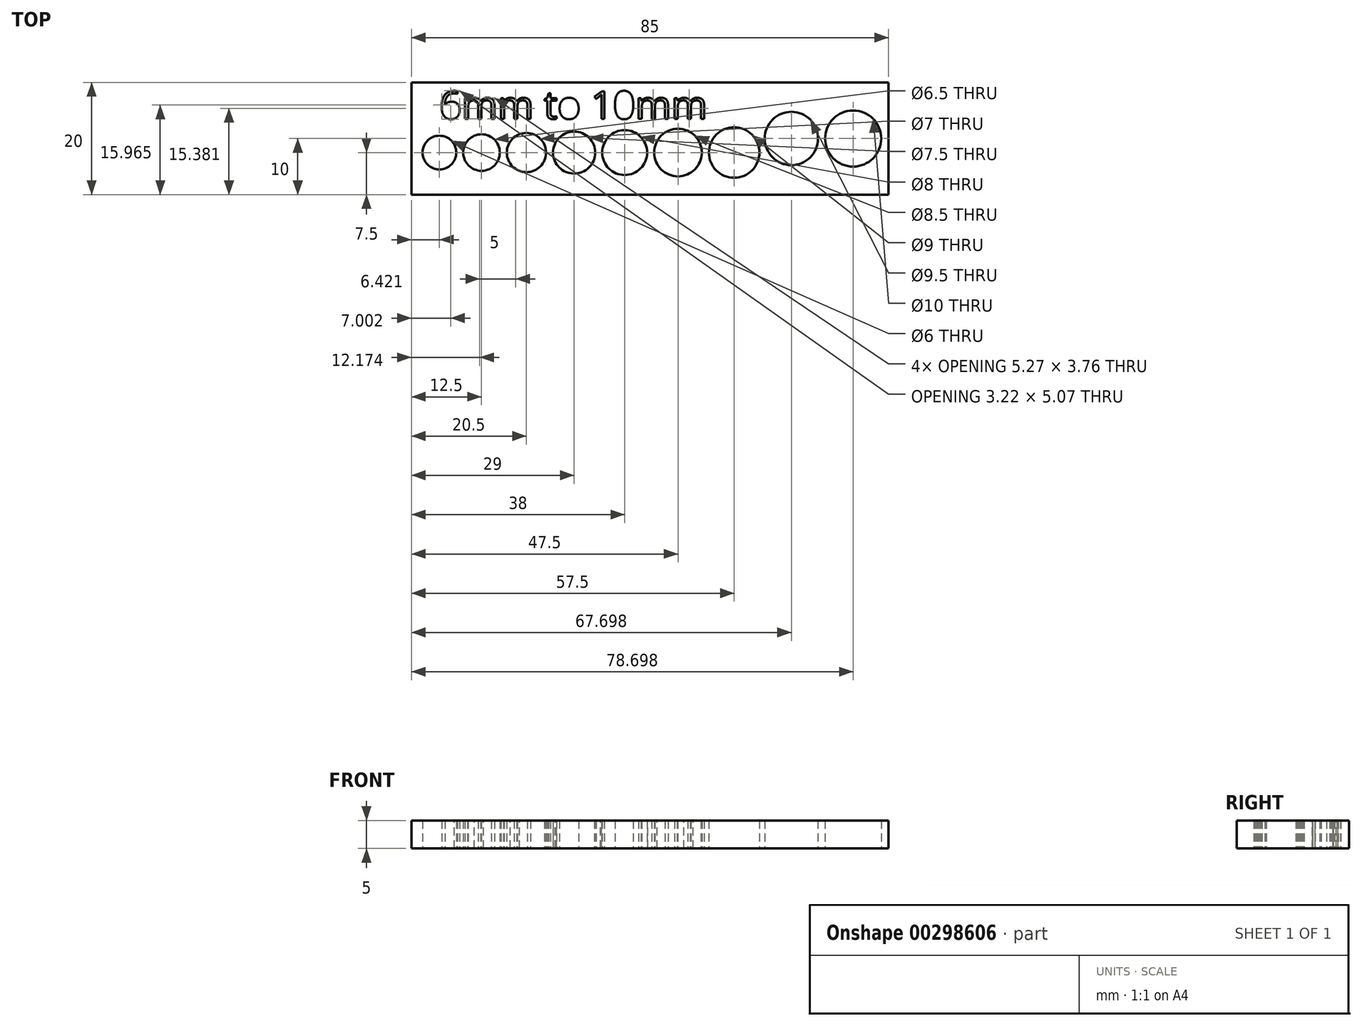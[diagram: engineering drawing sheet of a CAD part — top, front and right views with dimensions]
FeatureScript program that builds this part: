
annotation { "Feature Type Name" : "Feature", "Feature Type Description" : "" }
export const myFeature = defineFeature(function(context is Context, id is Id, definition is map)
    precondition{}
    {
        {
            var Q0;
            Q0=qCreatedBy(makeId("Top.planeOp"),FACE);
            var sketch = newSketch(context, id + "F0", { "sketchPlane" : qUnion([Q0])});
            skLineSegment(sketch, "E0.bottom", {"start": v(0, 0) * mm, "end": v(85, 0) * mm});
            skLineSegment(sketch, "E0.top", {"start": v(0, 20) * mm, "end": v(85, 20) * mm});
            skLineSegment(sketch, "E0.left", {"start": v(0, 0) * mm, "end": v(0, 20) * mm});
            skLineSegment(sketch, "E0.right", {"start": v(85, 0) * mm, "end": v(85, 20) * mm});
            skLineSegment(sketch, "E1", {"start": v(0, 7.5) * mm, "end": v(5, 7.5) * mm});
            skLineSegment(sketch, "E2", {"start": v(5, 7.5) * mm, "end": v(5, 0) * mm});
            skCircle(sketch, "E3", {"center": v(5, 7.5) * mm, "radius": 3 * mm});
            skLineSegment(sketch, "E4", {"start": v(5, 7.5) * mm, "end": v(12.5, 7.5) * mm});
            skLineSegment(sketch, "E5", {"start": v(12.5, 7.5) * mm, "end": v(20.5, 7.5) * mm});
            skLineSegment(sketch, "E6", {"start": v(20.5, 7.5) * mm, "end": v(29, 7.5) * mm});
            skCircle(sketch, "E7", {"center": v(12.5, 7.5) * mm, "radius": 3.25 * mm});
            skCircle(sketch, "E8", {"center": v(20.5, 7.5) * mm, "radius": 3.5 * mm});
            skCircle(sketch, "E9", {"center": v(29, 7.5) * mm, "radius": 3.75 * mm});
            skLineSegment(sketch, "E10", {"start": v(29, 7.5) * mm, "end": v(38, 7.5) * mm});
            skLineSegment(sketch, "E11", {"start": v(38, 7.5) * mm, "end": v(47.5, 7.5) * mm});
            skCircle(sketch, "E12", {"center": v(38, 7.5) * mm, "radius": 4 * mm});
            skCircle(sketch, "E13", {"center": v(47.5, 7.5) * mm, "radius": 4.25 * mm});
            skLineSegment(sketch, "E14", {"start": v(47.5, 7.5) * mm, "end": v(57.5, 7.5) * mm});
            skLineSegment(sketch, "E15", {"start": v(57.5, 7.5) * mm, "end": v(67.7, 10) * mm});
            skPoint(sketch, "E15.endSnap0", {"position": v(85, 10) * mm});
            skCircle(sketch, "E16", {"center": v(57.5, 7.5) * mm, "radius": 4.5 * mm});
            skCircle(sketch, "E17", {"center": v(67.7, 10) * mm, "radius": 4.75 * mm});
            skLineSegment(sketch, "E18", {"start": v(67.7, 10) * mm, "end": v(78.7, 10) * mm});
            skCircle(sketch, "E19", {"center": v(78.7, 10) * mm, "radius": 5 * mm});
            skLineSegment(sketch, "E20", {"start": v(5, 7.5) * mm, "end": v(5, 10.5) * mm});
            skLineSegment(sketch, "E21", {"start": v(5, 10.5) * mm, "end": v(5, 13.5) * mm});
            skText(sketch, "E22", { "text": "6mm to 10mm", "fontName": "OpenSans-Regular.ttf"});
            const initialGuessF0  = {"E22": [0.005, 0.0135, 1, 0, 0.00497]};
            skSetInitialGuess(sketch, initialGuessF0);
            skSolve(sketch);
        }
        {
            var Q0;
            Q0 = qSketchRegion(id + "F0", true);
            extrude(context, id + "F1", {"entities" : qUnion([Q0]), "depth" : 5 * mm});
        }
    });
